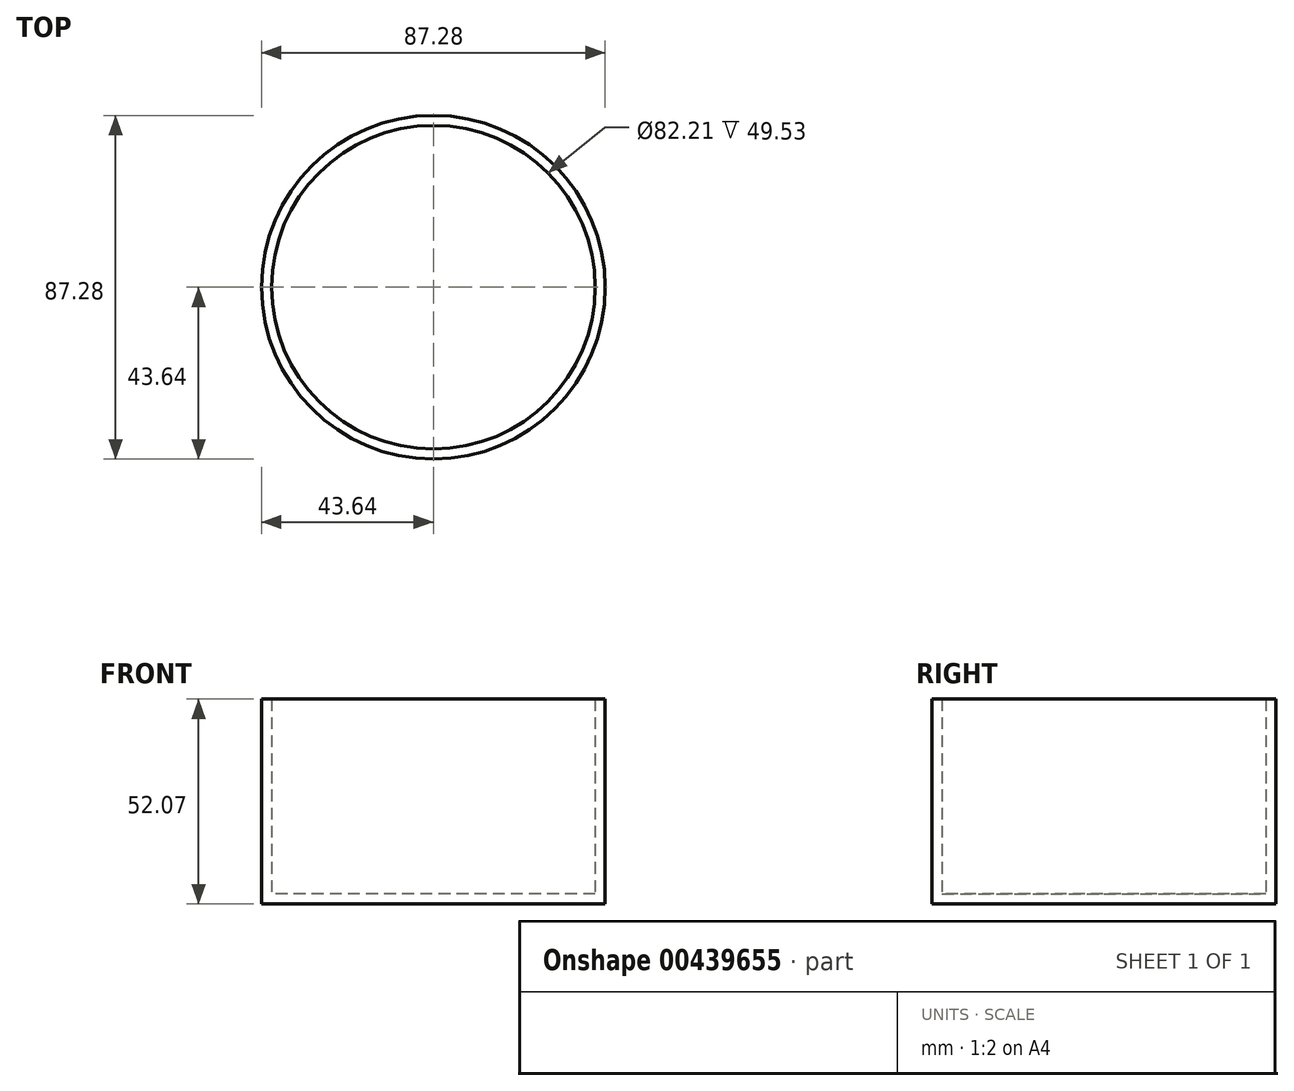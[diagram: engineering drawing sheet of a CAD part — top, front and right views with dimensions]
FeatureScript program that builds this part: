
annotation { "Feature Type Name" : "Feature", "Feature Type Description" : "" }
export const myFeature = defineFeature(function(context is Context, id is Id, definition is map)
    precondition{}
    {
        {
            var Q0;
            Q0=qCreatedBy(makeId("Top.planeOp"),FACE);
            var sketch = newSketch(context, id + "F0", { "sketchPlane" : qUnion([Q0])});
            skCircle(sketch, "E0", {"center": v(0, 0) * mm, "radius": 43.64 * mm});
            skSolve(sketch);
        }
        {
            var Q0;
            Q0=makeQuery(id+"F0.imprint","IMPRINT",FACE,{"disambiguationData":[TD([[makeQuery(id+"F0.imprint","IMPRINT",EDGE,{"derivedFrom":sQuery(id+"F0.wireOp",EDGE,"E0")}),1.0]])]});
            extrude(context, id + "F1", {"entities" : qUnion([Q0]), "depth" : 52.07 * mm});
        }
        {
            var Q0;
            Q0=makeQuery(id+"F1.opExtrude","CAP_FACE",FACE,{"disambiguationData":[OSD([sQuery(id+"F0.wireOp",EDGE,"E0")])],"isStart":false});
            shell(context, id + "F2", {"entities" : qUnion([Q0]), "thickness" : 2.54 * mm});
        }
        {
            var Q0;
            Q0=qCreatedBy(makeId("Top.planeOp"),FACE);
            cPlane(context, id + "F3", {"entities" : qUnion([Q0]), "cplaneType" : CPlaneType.OFFSET, "offset" : 96.27 * mm, "width" : 152.4 * mm, "height" : 152.4 * mm});
        }
    });
